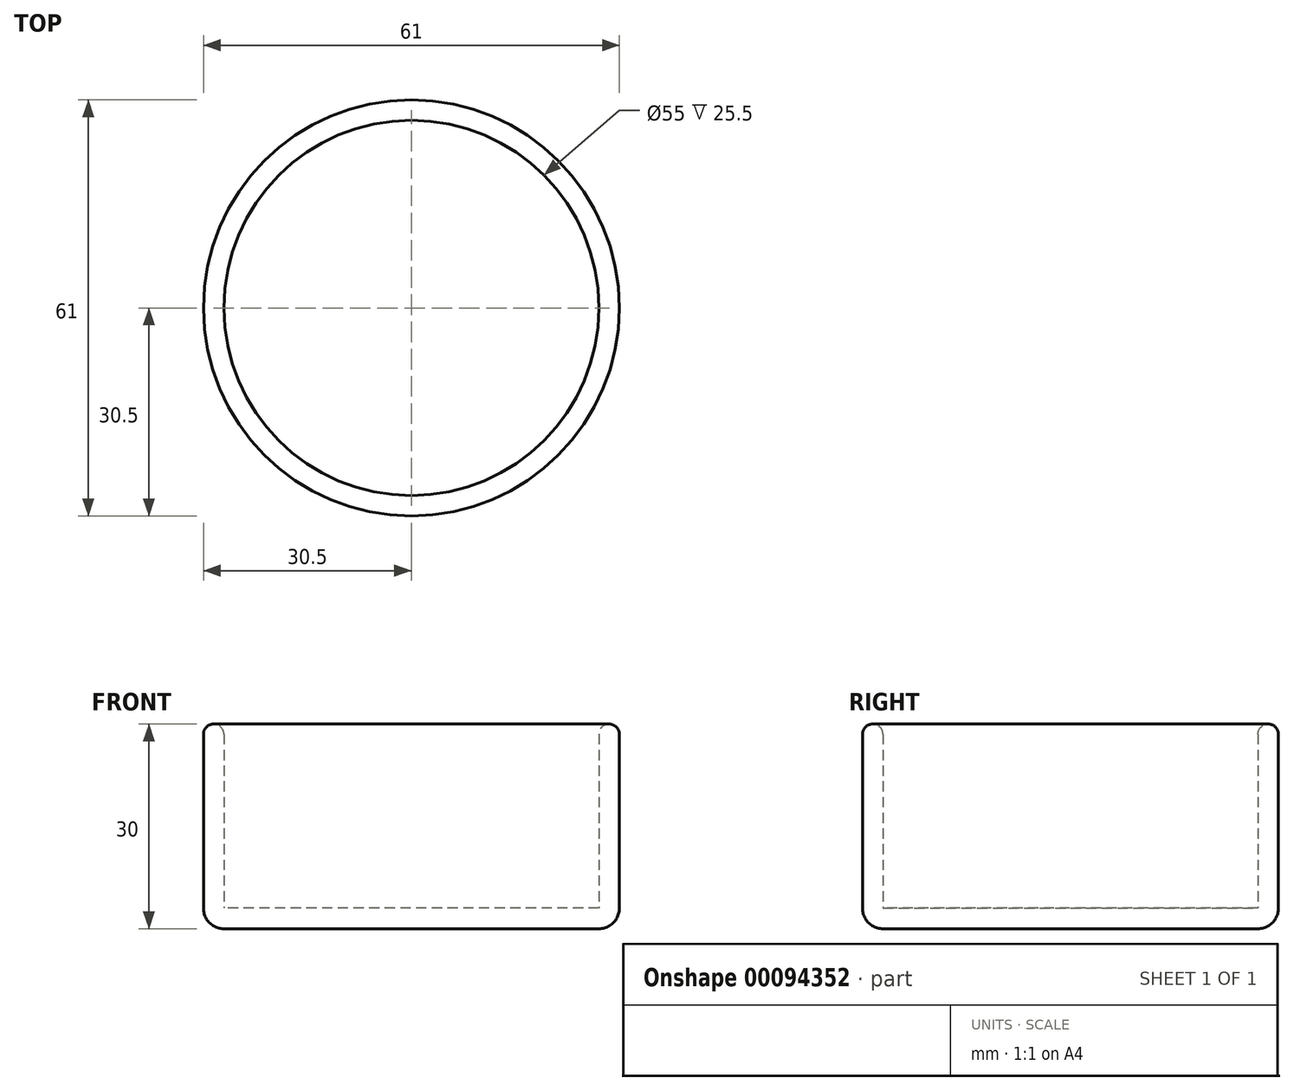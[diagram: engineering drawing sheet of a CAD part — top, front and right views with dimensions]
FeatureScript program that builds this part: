
annotation { "Feature Type Name" : "Feature", "Feature Type Description" : "" }
export const myFeature = defineFeature(function(context is Context, id is Id, definition is map)
    precondition{}
    {
        {
            var Q0;
            Q0=qCreatedBy(makeId("Top.planeOp"),FACE);
            var sketch = newSketch(context, id + "F0", { "sketchPlane" : qUnion([Q0])});
            skCircle(sketch, "E0", {"center": v(0, 0) * mm, "radius": 27.5 * mm});
            skCircle(sketch, "E1", {"center": v(0, 0) * mm, "radius": 30.5 * mm});
            skSolve(sketch);
        }
        {
            var Q0;
            Q0=makeQuery(id+"F0.imprint","IMPRINT",FACE,{"disambiguationData":[TD([[makeQuery(id+"F0.imprint","IMPRINT",EDGE,{"derivedFrom":sQuery(id+"F0.wireOp",EDGE,"E0")}),-1.0]])]});
            extrude(context, id + "F1", {"entities" : qUnion([Q0]), "depth" : 27 * mm});
        }
        {
            var Q0;
            Q0=makeQuery(id+"F0.imprint","IMPRINT",FACE,{"disambiguationData":[TD([[makeQuery(id+"F0.imprint","IMPRINT",EDGE,{"derivedFrom":sQuery(id+"F0.wireOp",EDGE,"E0")}),-1.0]])]});
            var Q1;
            Q1=makeQuery(id+"F0.imprint","IMPRINT",FACE,{"disambiguationData":[TD([[makeQuery(id+"F0.imprint","IMPRINT",EDGE,{"derivedFrom":sQuery(id+"F0.wireOp",EDGE,"E0")}),1.0]])]});
            extrude(context, id + "F2", {"entities" : qUnion([Q0, Q1]), "operationType" : NewBodyOperationType.ADD, "oppositeDirection" : true, "depth" : 3 * mm});
        }
        {
            var Q0;
            Q0=makeQuery(id+"F1.opExtrude","CAP_EDGE",EDGE,{"disambiguationData":[OSD([sQuery(id+"F0.wireOp",EDGE,"E1")])],"isStart":false});
            var Q1;
            Q1=makeQuery(id+"F1.opExtrude","CAP_EDGE",EDGE,{"disambiguationData":[OSD([sQuery(id+"F0.wireOp",EDGE,"E0")])],"isStart":false});
            var Q2;
            Q2=makeQuery(id+"F1.opExtrude","CAP_EDGE",EDGE,{"disambiguationData":[OSD([sQuery(id+"F0.wireOp",EDGE,"E0")])],"isStart":true});
            fillet(context, id + "F3", {"entities" : qUnion([Q0, Q1, Q2]), "radius" : 1.5 * mm, "tangentPropagation" : true, "allowEdgeOverflow" : false});
        }
        {
            var Q0;
            Q0=makeQuery(id+"F2.opExtrude","CAP_EDGE",EDGE,{"disambiguationData":[OSD([sQuery(id+"F0.wireOp",EDGE,"E1")])],"isStart":false});
            fillet(context, id + "F4", {"entities" : qUnion([Q0]), "radius" : 3 * mm, "tangentPropagation" : true, "allowEdgeOverflow" : false});
        }
    });
